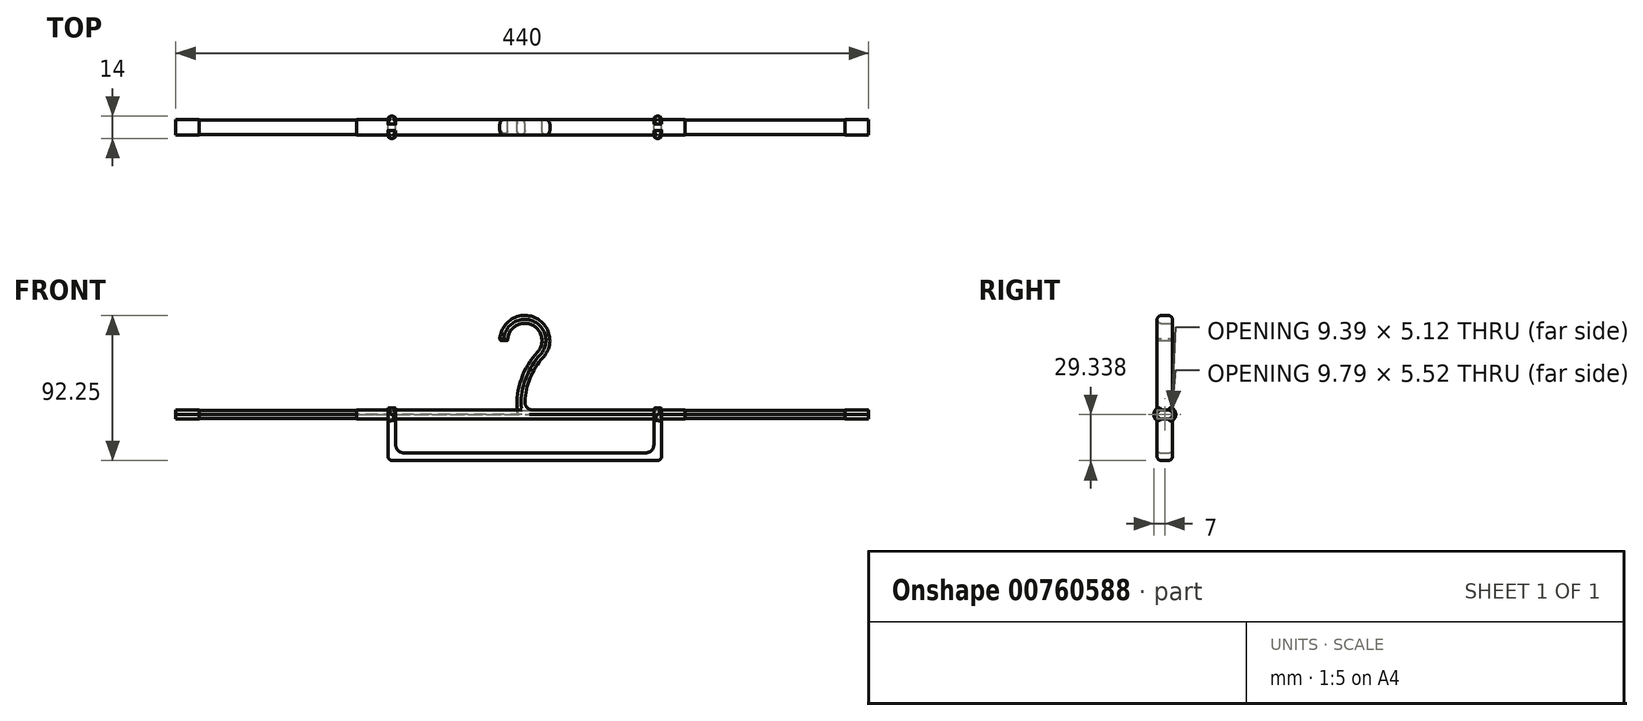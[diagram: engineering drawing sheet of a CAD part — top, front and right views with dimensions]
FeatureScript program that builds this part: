
annotation { "Feature Type Name" : "Feature", "Feature Type Description" : "" }
export const myFeature = defineFeature(function(context is Context, id is Id, definition is map)
    precondition{}
    {
        {
            var Q0;
            Q0=qCreatedBy(makeId("Front.planeOp"),FACE);
            var sketch = newSketch(context, id + "F0", { "sketchPlane" : qUnion([Q0])});
            skCircle(sketch, "E0", {"center": v(0, 49.86) * mm, "radius": 15.9 * mm});
            skCircle(sketch, "E1", {"center": v(0, 49.86) * mm, "radius": 10.9 * mm});
            skLineSegment(sketch, "E2", {"start": v(-15.9, 49.86) * mm, "end": v(-10.9, 49.86) * mm});
            skArc(sketch, "E3", {"start": v(11.73, 39.12) * mm, "mid": v(2.48, 23.62) * mm, "end": v(0.12, 5.72) * mm});
            skArc(sketch, "E4.0", {"start": v(8.04, 42.5) * mm, "mid": v(-2.18, 25.43) * mm, "end": v(-4.9, 5.72) * mm});
            skPoint(sketch, "E5.orphan", {"position": v(0, 9.1) * mm});
            skLineSegment(sketch, "E6", {"start": v(-4.9, 5.72) * mm, "end": v(0.12, 5.72) * mm});
            skLineSegment(sketch, "E7", {"start": v(-4.9, 5.72) * mm, "end": v(-106.71, 5.72) * mm});
            skLineSegment(sketch, "E8", {"start": v(-106.71, 5.72) * mm, "end": v(-106.71, 0) * mm});
            skLineSegment(sketch, "E9", {"start": v(-106.71, 0) * mm, "end": v(-2.39, 0) * mm});
            skPoint(sketch, "E9.endSnap0", {"position": v(-2.39, 5.72) * mm});
            skLineSegment(sketch, "E10", {"start": v(-2.39, 0) * mm, "end": v(-2.39, 5.72) * mm});
            skLineSegment(sketch, "E11.MirrorCS", {"start": v(0.12, 5.72) * mm, "end": v(101.93, 5.72) * mm});
            skLineSegment(sketch, "E12.MirrorCS", {"start": v(101.93, 5.72) * mm, "end": v(101.93, 0) * mm});
            skLineSegment(sketch, "E13.MirrorCS", {"start": v(101.93, 0) * mm, "end": v(-2.39, 0) * mm});
            skLineSegment(sketch, "E14", {"start": v(-86.94, 5.72) * mm, "end": v(-86.94, -26.48) * mm});
            skLineSegment(sketch, "E15", {"start": v(-86.94, -26.48) * mm, "end": v(0, -26.48) * mm});
            skLineSegment(sketch, "E16.0", {"start": v(-81.94, -21.48) * mm, "end": v(0, -21.48) * mm});
            skLineSegment(sketch, "E16.1", {"start": v(-81.94, 5.72) * mm, "end": v(-81.94, -21.48) * mm});
            skLineSegment(sketch, "E17.MirrorCS", {"start": v(81.94, -21.48) * mm, "end": v(0, -21.48) * mm});
            skLineSegment(sketch, "E18.MirrorCS", {"start": v(86.94, -26.48) * mm, "end": v(0, -26.48) * mm});
            skLineSegment(sketch, "E19.MirrorCS", {"start": v(81.94, 5.72) * mm, "end": v(81.94, -21.48) * mm});
            skLineSegment(sketch, "E20.MirrorCS", {"start": v(86.94, 5.72) * mm, "end": v(86.94, -26.48) * mm});
            skSolve(sketch);
        }
        {
            var Q0;
            {var subQ0=sQuery(id+"F0.wireOp",EDGE,"E2");Q0=makeQuery(id+"F0.imprint","IMPRINT",FACE,{"disambiguationData":[TD([[makeQuery(id+"F0.imprint","IMPRINT",EDGE,{"derivedFrom":subQ0}),1.0]])]});}
            var Q1;
            {var subQ6=sQuery(id+"F0.wireOp",EDGE,"E3");Q1=makeQuery(id+"F0.imprint","IMPRINT",FACE,{"disambiguationData":[TD([[makeQuery(id+"F0.imprint","IMPRINT",EDGE,{"derivedFrom":subQ6}),-1.0]])]});}
            extrude(context, id + "F1", {"entities" : qUnion([Q0, Q1]), "endBound" : BoundingType.SYMMETRIC, "depth" : 10 * mm, "offsetDistance" : 25 * mm});
        }
        {
            var Q0;
            {var subQ0=sQuery(id+"F0.wireOp",EDGE,"E10");Q0=makeQuery(id+"F0.imprint","IMPRINT",FACE,{"disambiguationData":[TD([[makeQuery(id+"F0.imprint","IMPRINT",EDGE,{"derivedFrom":subQ0}),1.0]])]});}
            var Q1;
            {var subQ5=sQuery(id+"F0.wireOp",EDGE,"E10");Q1=makeQuery(id+"F0.imprint","IMPRINT",FACE,{"disambiguationData":[TD([[makeQuery(id+"F0.imprint","IMPRINT",EDGE,{"derivedFrom":subQ5}),-1.0]])]});}
            var Q2;
            {var subQ0=sQuery(id+"F0.wireOp",EDGE,"E14");var subQ1=sQuery(id+"F0.wireOp",EDGE,"E7");var subQ2=makeQuery(id+"F0.imprint","INTERSECT",VERTEX,{"derivedFrom":[subQ1,subQ0]});Q2=makeQuery(id+"F0.imprint","IMPRINT",FACE,{"disambiguationData":[TD([[makeQuery(id+"F0.imprint","IMPRINT",EDGE,{"disambiguationData":[TD([[subQ2,1.0]])],"derivedFrom":subQ1}),1.0]])]});}
            var Q3;
            {var subQ0=sQuery(id+"F0.wireOp",EDGE,"E8");Q3=makeQuery(id+"F0.imprint","IMPRINT",FACE,{"disambiguationData":[TD([[makeQuery(id+"F0.imprint","IMPRINT",EDGE,{"derivedFrom":subQ0}),1.0]])]});}
            var Q4;
            {var subQ0=sQuery(id+"F0.wireOp",EDGE,"E19.MirrorCS");var subQ1=sQuery(id+"F0.wireOp",EDGE,"E11.MirrorCS");var subQ2=makeQuery(id+"F0.imprint","INTERSECT",VERTEX,{"derivedFrom":[subQ1,subQ0]});Q4=makeQuery(id+"F0.imprint","IMPRINT",FACE,{"disambiguationData":[TD([[makeQuery(id+"F0.imprint","IMPRINT",EDGE,{"disambiguationData":[TD([[subQ2,-1.0]])],"derivedFrom":subQ1}),-1.0]])]});}
            var Q5;
            {var subQ0=sQuery(id+"F0.wireOp",EDGE,"E12.MirrorCS");Q5=makeQuery(id+"F0.imprint","IMPRINT",FACE,{"disambiguationData":[TD([[makeQuery(id+"F0.imprint","IMPRINT",EDGE,{"derivedFrom":subQ0}),-1.0]])]});}
            extrude(context, id + "F2", {"entities" : qUnion([Q0, Q1, Q2, Q3, Q4, Q5]), "endBound" : BoundingType.SYMMETRIC, "depth" : 10 * mm, "offsetDistance" : 25 * mm});
        }
        {
            var Q0;
            Q0=makeQuery(id+"F1.opExtrude","SWEPT_BODY",BODY,{"disambiguationData":[OSD([sQuery(id+"F0.wireOp",EDGE,"E0"),sQuery(id+"F0.wireOp",EDGE,"E1"),sQuery(id+"F0.wireOp",EDGE,"E2"),sQuery(id+"F0.wireOp",EDGE,"E3"),sQuery(id+"F0.wireOp",EDGE,"E4.0"),sQuery(id+"F0.wireOp",EDGE,"E6")])]});
            var Q1;
            Q1=makeQuery(id+"F2.opExtrude","SWEPT_BODY",BODY,{"disambiguationData":[OSD([sQuery(id+"F0.wireOp",EDGE,"E6"),sQuery(id+"F0.wireOp",EDGE,"E7"),sQuery(id+"F0.wireOp",EDGE,"E8"),sQuery(id+"F0.wireOp",EDGE,"E9"),sQuery(id+"F0.wireOp",EDGE,"E11.MirrorCS"),sQuery(id+"F0.wireOp",EDGE,"E12.MirrorCS"),sQuery(id+"F0.wireOp",EDGE,"E13.MirrorCS")])]});
            booleanBodies(context, id + "F3", {"operationType" : BooleanOperationType.UNION, "tools" : qUnion([Q0, Q1])});
        }
        {
            var Q0;
            {var subQ0=sQuery(id+"F0.wireOp",EDGE,"E15");Q0=makeQuery(id+"F0.imprint","IMPRINT",FACE,{"disambiguationData":[TD([[makeQuery(id+"F0.imprint","IMPRINT",EDGE,{"derivedFrom":subQ0}),1.0]])]});}
            extrude(context, id + "F4", {"entities" : qUnion([Q0]), "endBound" : BoundingType.SYMMETRIC, "depth" : 10 * mm, "offsetDistance" : 25 * mm});
        }
        {
            var Q0;
            Q0=makeQuery(id+"F1.opExtrude","SWEPT_EDGE",EDGE,{"disambiguationData":[OSD([sQuery(id+"F0.wireOp",EDGE,"E4.0"),sQuery(id+"F0.wireOp",EDGE,"E6"),sQuery(id+"F0.wireOp",EDGE,"E7")])]});
            var Q1;
            Q1=makeQuery(id+"F1.opExtrude","SWEPT_EDGE",EDGE,{"disambiguationData":[OSD([sQuery(id+"F0.wireOp",EDGE,"E3"),sQuery(id+"F0.wireOp",EDGE,"E6"),sQuery(id+"F0.wireOp",EDGE,"E11.MirrorCS")])]});
            fillet(context, id + "F5", {"entities" : qUnion([Q0, Q1]), "radius" : 5 * mm, "tangentPropagation" : true, "allowEdgeOverflow" : false});
        }
        {
            var Q0;
            Q0=makeQuery(id+"F1.opExtrude","CAP_EDGE",EDGE,{"disambiguationData":[OSD([sQuery(id+"F0.wireOp",EDGE,"E4.0")])],"isStart":false});
            var Q1;
            Q1=makeQuery(id+"F1.opExtrude","CAP_EDGE",EDGE,{"disambiguationData":[OSD([sQuery(id+"F0.wireOp",EDGE,"E3")])],"isStart":false});
            fillet(context, id + "F6", {"entities" : qUnion([Q0, Q1]), "radius" : 3 * mm, "tangentPropagation" : true, "allowEdgeOverflow" : false});
        }
        {
            var Q0;
            {var subQ0=sQuery(id+"F0.wireOp",EDGE,"E11.MirrorCS");var subQ1=sQuery(id+"F0.wireOp",EDGE,"E7");var subQ2=sQuery(id+"F0.wireOp",EDGE,"E6");var subQ3=sQuery(id+"F0.wireOp",EDGE,"E4.0");Q0=makeQuery(id+"F3.opBoolean","SPLIT",EDGE,{"disambiguationData":[TD([makeQuery(id+"F1.opExtrude","SWEPT_FACE",FACE,{"disambiguationData":[OSD([subQ3])]})])],"derivedFrom":makeQuery(id+"F2.opExtrude","CAP_EDGE",EDGE,{"disambiguationData":[OSD([subQ2,subQ1,subQ0])],"isStart":true})});}
            var Q1;
            Q1=makeQuery(id+"F1.opExtrude","CAP_EDGE",EDGE,{"disambiguationData":[OSD([sQuery(id+"F0.wireOp",EDGE,"E0")])],"isStart":true});
            fillet(context, id + "F7", {"entities" : qUnion([Q0, Q1]), "radius" : 3 * mm, "tangentPropagation" : true, "allowEdgeOverflow" : false});
        }
        {
            var Q0;
            Q0=makeQuery(id+"F2.opExtrude","CAP_EDGE",EDGE,{"disambiguationData":[OSD([sQuery(id+"F0.wireOp",EDGE,"E9"),sQuery(id+"F0.wireOp",EDGE,"E13.MirrorCS")])],"isStart":false});
            var Q1;
            Q1=makeQuery(id+"F2.opExtrude","CAP_EDGE",EDGE,{"disambiguationData":[OSD([sQuery(id+"F0.wireOp",EDGE,"E9"),sQuery(id+"F0.wireOp",EDGE,"E13.MirrorCS")])],"isStart":true});
            fillet(context, id + "F8", {"entities" : qUnion([Q0, Q1]), "radius" : 3 * mm, "tangentPropagation" : true, "allowEdgeOverflow" : false});
        }
        {
            var Q0;
            Q0=makeQuery(id+"F4.opExtrude","CAP_EDGE",EDGE,{"disambiguationData":[OSD([sQuery(id+"F0.wireOp",EDGE,"E14")])],"isStart":false});
            var Q1;
            Q1=makeQuery(id+"F4.opExtrude","CAP_EDGE",EDGE,{"disambiguationData":[OSD([sQuery(id+"F0.wireOp",EDGE,"E14")])],"isStart":true});
            var Q2;
            Q2=makeQuery(id+"F4.opExtrude","CAP_EDGE",EDGE,{"disambiguationData":[OSD([sQuery(id+"F0.wireOp",EDGE,"E15"),sQuery(id+"F0.wireOp",EDGE,"E18.MirrorCS")])],"isStart":false});
            var Q3;
            Q3=makeQuery(id+"F4.opExtrude","CAP_EDGE",EDGE,{"disambiguationData":[OSD([sQuery(id+"F0.wireOp",EDGE,"E15"),sQuery(id+"F0.wireOp",EDGE,"E18.MirrorCS")])],"isStart":true});
            var Q4;
            Q4=makeQuery(id+"F4.opExtrude","CAP_EDGE",EDGE,{"disambiguationData":[OSD([sQuery(id+"F0.wireOp",EDGE,"E20.MirrorCS")])],"isStart":false});
            var Q5;
            Q5=makeQuery(id+"F4.opExtrude","CAP_EDGE",EDGE,{"disambiguationData":[OSD([sQuery(id+"F0.wireOp",EDGE,"E20.MirrorCS")])],"isStart":true});
            var Q6;
            Q6=makeQuery(id+"F4.opExtrude","SWEPT_EDGE",EDGE,{"disambiguationData":[OSD([sQuery(id+"F0.wireOp",EDGE,"E18.MirrorCS"),sQuery(id+"F0.wireOp",EDGE,"E20.MirrorCS")])]});
            var Q7;
            Q7=makeQuery(id+"F4.opExtrude","SWEPT_EDGE",EDGE,{"disambiguationData":[OSD([sQuery(id+"F0.wireOp",EDGE,"E14"),sQuery(id+"F0.wireOp",EDGE,"E15")])]});
            fillet(context, id + "F9", {"entities" : qUnion([Q0, Q1, Q2, Q3, Q4, Q5, Q6, Q7]), "radius" : 3 * mm, "tangentPropagation" : true, "allowEdgeOverflow" : false});
        }
        {
            var Q0;
            Q0=makeQuery(id+"F4.opExtrude","SWEPT_EDGE",EDGE,{"disambiguationData":[OSD([sQuery(id+"F0.wireOp",EDGE,"E16.0"),sQuery(id+"F0.wireOp",EDGE,"E16.1")])]});
            var Q1;
            Q1=makeQuery(id+"F4.opExtrude","SWEPT_EDGE",EDGE,{"disambiguationData":[OSD([sQuery(id+"F0.wireOp",EDGE,"E17.MirrorCS"),sQuery(id+"F0.wireOp",EDGE,"E19.MirrorCS")])]});
            fillet(context, id + "F10", {"entities" : qUnion([Q0, Q1]), "radius" : 5 * mm, "tangentPropagation" : true, "allowEdgeOverflow" : false});
        }
        {
            var Q0;
            Q0=makeQuery(id+"F4.opExtrude","CAP_EDGE",EDGE,{"disambiguationData":[OSD([sQuery(id+"F0.wireOp",EDGE,"E16.1")])],"isStart":false});
            var Q1;
            Q1=makeQuery(id+"F4.opExtrude","CAP_EDGE",EDGE,{"disambiguationData":[OSD([sQuery(id+"F0.wireOp",EDGE,"E19.MirrorCS")])],"isStart":true});
            fillet(context, id + "F11", {"entities" : qUnion([Q0, Q1]), "radius" : 2 * mm, "tangentPropagation" : true, "allowEdgeOverflow" : false});
        }
        {
            var Q0;
            Q0=makeQuery(id+"F2.opExtrude","SWEPT_FACE",FACE,{"disambiguationData":[OSD([sQuery(id+"F0.wireOp",EDGE,"E8")])]});
            var sketch = newSketch(context, id + "F12", { "sketchPlane" : qUnion([Q0])});
            skLineSegment(sketch, "E21.0", {"start": v(2, 5.62) * mm, "end": v(-2, 5.62) * mm});
            skArc(sketch, "E21.1", {"start": v(-4.9, 2.86) * mm, "mid": v(-4, 0.9) * mm, "end": v(-2, 0.1) * mm});
            skLineSegment(sketch, "E21.2", {"start": v(-2, 0.1) * mm, "end": v(2, 0.1) * mm});
            skArc(sketch, "E21.3", {"start": v(-2, 5.62) * mm, "mid": v(-4, 4.82) * mm, "end": v(-4.9, 2.86) * mm});
            skArc(sketch, "E21.4", {"start": v(2, 0.1) * mm, "mid": v(4, 0.9) * mm, "end": v(4.9, 2.86) * mm});
            skArc(sketch, "E21.5", {"start": v(4.9, 2.86) * mm, "mid": v(4, 4.82) * mm, "end": v(2, 5.62) * mm});
            skSolve(sketch);
        }
        {
            var Q0;
            Q0=makeQuery(id+"F12.imprint","IMPRINT",FACE,{"disambiguationData":[TD([[makeQuery(id+"F12.imprint","IMPRINT",EDGE,{"derivedFrom":sQuery(id+"F12.wireOp",EDGE,"E21.0")}),1.0]])]});
            extrude(context, id + "F13", {"entities" : qUnion([Q0]), "operationType" : NewBodyOperationType.REMOVE, "oppositeDirection" : true, "depth" : 250 * mm, "offsetDistance" : 25 * mm});
        }
        {
            var Q0;
            Q0=makeQuery(id+"F12.imprint","IMPRINT",FACE,{"disambiguationData":[TD([[makeQuery(id+"F12.imprint","IMPRINT",EDGE,{"derivedFrom":sQuery(id+"F12.wireOp",EDGE,"E21.0")}),-1.0]])]});
            var sketch = newSketch(context, id + "F14", { "sketchPlane" : qUnion([Q0])});
            skArc(sketch, "E22.0", {"start": v(-4.7, 2.86) * mm, "mid": v(-3.86, 1.04) * mm, "end": v(-2, 0.3) * mm});
            skArc(sketch, "E22.1", {"start": v(2, 0.3) * mm, "mid": v(3.86, 1.04) * mm, "end": v(4.7, 2.86) * mm});
            skArc(sketch, "E22.2", {"start": v(4.7, 2.86) * mm, "mid": v(3.86, 4.68) * mm, "end": v(2, 5.42) * mm});
            skLineSegment(sketch, "E22.3", {"start": v(-2, 0.3) * mm, "end": v(2, 0.3) * mm});
            skLineSegment(sketch, "E22.4", {"start": v(2, 5.42) * mm, "end": v(-2, 5.42) * mm});
            skArc(sketch, "E22.5", {"start": v(-2, 5.42) * mm, "mid": v(-3.86, 4.68) * mm, "end": v(-4.7, 2.86) * mm});
            skSolve(sketch);
        }
        {
            var Q0;
            Q0=makeQuery(id+"F14.imprint","IMPRINT",FACE,{"disambiguationData":[TD([[makeQuery(id+"F14.imprint","IMPRINT",EDGE,{"derivedFrom":sQuery(id+"F14.wireOp",EDGE,"E22.0")}),1.0]])]});
            extrude(context, id + "F15", {"entities" : qUnion([Q0]), "depth" : 100 * mm, "offsetDistance" : 25 * mm});
        }
        {
            var Q0;
            Q0=makeQuery(id+"F14.imprint","IMPRINT",FACE,{"disambiguationData":[TD([[makeQuery(id+"F14.imprint","IMPRINT",EDGE,{"derivedFrom":sQuery(id+"F14.wireOp",EDGE,"E22.0")}),1.0]])]});
            extrude(context, id + "F16", {"entities" : qUnion([Q0]), "operationType" : NewBodyOperationType.ADD, "oppositeDirection" : true, "depth" : 310 * mm, "offsetDistance" : 25 * mm});
        }
        {
            var Q0;
            Q0=makeQuery(id+"F15.opExtrude","CAP_FACE",FACE,{"disambiguationData":[OSD([sQuery(id+"F14.wireOp",EDGE,"E22.0"),sQuery(id+"F14.wireOp",EDGE,"E22.1"),sQuery(id+"F14.wireOp",EDGE,"E22.2"),sQuery(id+"F14.wireOp",EDGE,"E22.3"),sQuery(id+"F14.wireOp",EDGE,"E22.4"),sQuery(id+"F14.wireOp",EDGE,"E22.5")])],"isStart":false});
            var sketch = newSketch(context, id + "F17", { "sketchPlane" : qUnion([Q0])});
            skArc(sketch, "E23.0", {"start": v(-2, 5.62) * mm, "mid": v(-4, 4.82) * mm, "end": v(-4.9, 2.86) * mm});
            skLineSegment(sketch, "E24.0", {"start": v(2, 5.62) * mm, "end": v(-2, 5.62) * mm});
            skArc(sketch, "E25.0", {"start": v(4.9, 2.86) * mm, "mid": v(4, 4.82) * mm, "end": v(2, 5.62) * mm});
            skArc(sketch, "E26.0", {"start": v(2, 0.1) * mm, "mid": v(4, 0.9) * mm, "end": v(4.9, 2.86) * mm});
            skLineSegment(sketch, "E27.0", {"start": v(-2, 0.1) * mm, "end": v(2, 0.1) * mm});
            skArc(sketch, "E28.0", {"start": v(-4.9, 2.86) * mm, "mid": v(-4, 0.9) * mm, "end": v(-2, 0.1) * mm});
            skSolve(sketch);
        }
        {
            var Q0;
            Q0 = qSketchRegion(id + "F17", true);
            extrude(context, id + "F18", {"entities" : qUnion([Q0]), "operationType" : NewBodyOperationType.ADD, "depth" : 5 * mm, "offsetDistance" : 25 * mm});
        }
        {
            var Q0;
            Q0=makeQuery(id+"F16.opExtrude","CAP_FACE",FACE,{"disambiguationData":[OSD([sQuery(id+"F14.wireOp",EDGE,"E22.0"),sQuery(id+"F14.wireOp",EDGE,"E22.1"),sQuery(id+"F14.wireOp",EDGE,"E22.2"),sQuery(id+"F14.wireOp",EDGE,"E22.3"),sQuery(id+"F14.wireOp",EDGE,"E22.4"),sQuery(id+"F14.wireOp",EDGE,"E22.5")])],"isStart":false});
            var sketch = newSketch(context, id + "F19", { "sketchPlane" : qUnion([Q0])});
            skArc(sketch, "E29.0", {"start": v(-2, 5.72) * mm, "mid": v(-4.07, 4.89) * mm, "end": v(-5, 2.86) * mm});
            skLineSegment(sketch, "E30.0", {"start": v(-2, 5.72) * mm, "end": v(2, 5.72) * mm});
            skArc(sketch, "E31.0", {"start": v(5, 2.86) * mm, "mid": v(4.07, 4.89) * mm, "end": v(2, 5.72) * mm});
            skArc(sketch, "E32.0", {"start": v(2, 0) * mm, "mid": v(4.07, 0.83) * mm, "end": v(5, 2.86) * mm});
            skLineSegment(sketch, "E33.0", {"start": v(2, 0.1) * mm, "end": v(-2, 0.1) * mm});
            skArc(sketch, "E34.0", {"start": v(-5, 2.86) * mm, "mid": v(-4.07, 0.83) * mm, "end": v(-2, 0) * mm});
            skLineSegment(sketch, "E35.0", {"start": v(-2, 0) * mm, "end": v(2, 0) * mm});
            skSolve(sketch);
        }
        {
            var Q0;
            Q0 = qSketchRegion(id + "F19", true);
            extrude(context, id + "F20", {"entities" : qUnion([Q0]), "operationType" : NewBodyOperationType.ADD, "depth" : 5 * mm, "offsetDistance" : 25 * mm});
        }
        {
            var Q0;
            Q0=makeQuery(id+"F4.opExtrude","SWEPT_FACE",FACE,{"disambiguationData":[OSD([sQuery(id+"F0.wireOp",EDGE,"E14")])]});
            var sketch = newSketch(context, id + "F21", { "sketchPlane" : qUnion([Q0])});
            skLineSegment(sketch, "E36.0", {"start": v(2, 5.72) * mm, "end": v(-2, 5.72) * mm});
            skArc(sketch, "E37.0", {"start": v(-2, 5.72) * mm, "mid": v(-4.07, 4.89) * mm, "end": v(-5, 2.86) * mm});
            skArc(sketch, "E38.0", {"start": v(-5, 2.86) * mm, "mid": v(-4.07, 0.83) * mm, "end": v(-2, 0) * mm});
            skLineSegment(sketch, "E39.0", {"start": v(2, 0) * mm, "end": v(-2, 0) * mm});
            skArc(sketch, "E40.0", {"start": v(2, 0) * mm, "mid": v(4.07, 0.83) * mm, "end": v(5, 2.86) * mm});
            skArc(sketch, "E41.0", {"start": v(5, 2.86) * mm, "mid": v(4.07, 4.89) * mm, "end": v(2, 5.72) * mm});
            skArc(sketch, "E42.0", {"start": v(7, 2.86) * mm, "mid": v(5.49, 6.3) * mm, "end": v(2, 7.72) * mm});
            skArc(sketch, "E42.1", {"start": v(-2, 7.72) * mm, "mid": v(-5.49, 6.3) * mm, "end": v(-7, 2.86) * mm});
            skArc(sketch, "E42.2", {"start": v(-7, 2.86) * mm, "mid": v(-5.49, -0.59) * mm, "end": v(-2, -2) * mm});
            skLineSegment(sketch, "E42.3", {"start": v(2, -2) * mm, "end": v(-2, -2) * mm});
            skArc(sketch, "E42.4", {"start": v(2, -2) * mm, "mid": v(5.49, -0.59) * mm, "end": v(7, 2.86) * mm});
            skLineSegment(sketch, "E43", {"start": v(-2, 7.72) * mm, "end": v(-2, 5.72) * mm});
            skLineSegment(sketch, "E44", {"start": v(2, 7.72) * mm, "end": v(2, 5.72) * mm});
            skSolve(sketch);
        }
        {
            var Q0;
            {var subQ0=sQuery(id+"F21.wireOp",EDGE,"E40.0");Q0=makeQuery(id+"F21.imprint","IMPRINT",FACE,{"disambiguationData":[TD([[makeQuery(id+"F21.imprint","IMPRINT",EDGE,{"derivedFrom":subQ0}),-1.0]])]});}
            var Q1;
            {var subQ0=sQuery(id+"F21.wireOp",EDGE,"E39.0");Q1=makeQuery(id+"F21.imprint","IMPRINT",FACE,{"disambiguationData":[TD([[makeQuery(id+"F21.imprint","IMPRINT",EDGE,{"derivedFrom":subQ0}),1.0]])]});}
            var Q2;
            Q2=makeQuery(id+"F21.imprint","IMPRINT",FACE,{"disambiguationData":[TD([[makeQuery(id+"F21.imprint","IMPRINT",EDGE,{"derivedFrom":sQuery(id+"F21.wireOp",EDGE,"E37.0")}),-1.0]])]});
            extrude(context, id + "F22", {"entities" : qUnion([Q0, Q1, Q2]), "operationType" : NewBodyOperationType.ADD, "oppositeDirection" : true, "depth" : 5 * mm, "offsetDistance" : 25 * mm});
        }
        {
            var Q0;
            Q0=makeQuery(id+"F4.opExtrude","SWEPT_FACE",FACE,{"disambiguationData":[OSD([sQuery(id+"F0.wireOp",EDGE,"E20.MirrorCS")])]});
            var sketch = newSketch(context, id + "F23", { "sketchPlane" : qUnion([Q0])});
            skArc(sketch, "E45.0.0", {"start": v(-7, 2.86) * mm, "mid": v(-5.83, -0.22) * mm, "end": v(-3, -1.9) * mm});
            skArc(sketch, "E45.0.4", {"start": v(3, -1.9) * mm, "mid": v(5.83, -0.22) * mm, "end": v(7, 2.86) * mm});
            skArc(sketch, "E45.0.5", {"start": v(7, 2.86) * mm, "mid": v(5.49, 6.3) * mm, "end": v(2, 7.72) * mm});
            skLineSegment(sketch, "E45.0.6", {"start": v(2, 7.72) * mm, "end": v(2, 5.72) * mm});
            skArc(sketch, "E45.0.7", {"start": v(2, 5.72) * mm, "mid": v(4.07, 4.89) * mm, "end": v(5, 2.86) * mm});
            skArc(sketch, "E45.0.8", {"start": v(5, 2.86) * mm, "mid": v(4.07, 0.83) * mm, "end": v(2, 0) * mm});
            skLineSegment(sketch, "E45.0.9", {"start": v(2, 0) * mm, "end": v(-2, 0) * mm});
            skArc(sketch, "E45.0.10", {"start": v(-2, 0) * mm, "mid": v(-4.07, 0.83) * mm, "end": v(-5, 2.86) * mm});
            skArc(sketch, "E45.0.11", {"start": v(-5, 2.86) * mm, "mid": v(-4.07, 4.89) * mm, "end": v(-2, 5.72) * mm});
            skLineSegment(sketch, "E45.0.12", {"start": v(-2, 5.72) * mm, "end": v(-2, 7.72) * mm});
            skArc(sketch, "E45.0.13", {"start": v(-2, 7.72) * mm, "mid": v(-5.49, 6.3) * mm, "end": v(-7, 2.86) * mm});
            skArc(sketch, "E46.0", {"start": v(-2, -2) * mm, "mid": v(-5.45, -0.62) * mm, "end": v(-7, 2.76) * mm});
            skLineSegment(sketch, "E46.1", {"start": v(2, -2) * mm, "end": v(-2, -2) * mm});
            skArc(sketch, "E46.2", {"start": v(7, 2.76) * mm, "mid": v(5.45, -0.62) * mm, "end": v(2, -2) * mm});
            skSolve(sketch);
        }
        {
            var Q0;
            {var subQ5=sQuery(id+"F23.wireOp",EDGE,"E45.0.0");Q0=makeQuery(id+"F23.imprint","IMPRINT",FACE,{"disambiguationData":[TD([[makeQuery(id+"F23.imprint","IMPRINT",EDGE,{"derivedFrom":subQ5}),1.0]])]});}
            var Q1;
            {var subQ0=sQuery(id+"F23.wireOp",EDGE,"E45.0.9");Q1=makeQuery(id+"F23.imprint","IMPRINT",FACE,{"disambiguationData":[TD([[makeQuery(id+"F23.imprint","IMPRINT",EDGE,{"derivedFrom":subQ0}),-1.0]])]});}
            var Q2;
            {var subQ1=sQuery(id+"F23.wireOp",EDGE,"E45.0.4");Q2=makeQuery(id+"F23.imprint","IMPRINT",FACE,{"disambiguationData":[TD([[makeQuery(id+"F23.imprint","IMPRINT",EDGE,{"derivedFrom":subQ1}),1.0]])]});}
            extrude(context, id + "F24", {"entities" : qUnion([Q0, Q1, Q2]), "operationType" : NewBodyOperationType.ADD, "oppositeDirection" : true, "depth" : 5 * mm, "offsetDistance" : 25 * mm});
        }
        {
            var Q0;
            Q0=makeQuery(id+"F22.opExtrude","CAP_EDGE",EDGE,{"disambiguationData":[OSD([sQuery(id+"F21.wireOp",EDGE,"E42.4")])],"isStart":true});
            var Q1;
            Q1=makeQuery(id+"F22.opExtrude","CAP_EDGE",EDGE,{"disambiguationData":[OSD([sQuery(id+"F21.wireOp",EDGE,"E42.0")])],"isStart":false});
            var Q2;
            Q2=makeQuery(id+"F22.opExtrude","CAP_EDGE",EDGE,{"disambiguationData":[OSD([sQuery(id+"F21.wireOp",EDGE,"E42.2")])],"isStart":true});
            var Q3;
            Q3=makeQuery(id+"F22.opExtrude","CAP_EDGE",EDGE,{"disambiguationData":[OSD([sQuery(id+"F21.wireOp",EDGE,"E42.2")])],"isStart":false});
            var Q4;
            Q4=makeQuery(id+"F24.opExtrude","CAP_EDGE",EDGE,{"disambiguationData":[OSD([sQuery(id+"F23.wireOp",EDGE,"E45.0.13")])],"isStart":false});
            var Q5;
            Q5=makeQuery(id+"F24.opExtrude","CAP_EDGE",EDGE,{"disambiguationData":[OSD([sQuery(id+"F23.wireOp",EDGE,"E45.0.0"),sQuery(id+"F23.wireOp",EDGE,"E46.0")])],"isStart":true});
            var Q6;
            Q6=makeQuery(id+"F24.opExtrude","CAP_EDGE",EDGE,{"disambiguationData":[OSD([sQuery(id+"F23.wireOp",EDGE,"E45.0.5")])],"isStart":false});
            var Q7;
            Q7=makeQuery(id+"F24.opExtrude","CAP_EDGE",EDGE,{"disambiguationData":[OSD([sQuery(id+"F23.wireOp",EDGE,"E45.0.5")])],"isStart":true});
            var Q8;
            Q8=makeQuery(id+"F24.opExtrude","SWEPT_EDGE",EDGE,{"disambiguationData":[OSD([sQuery(id+"F23.wireOp",EDGE,"E45.0.5"),sQuery(id+"F23.wireOp",EDGE,"E45.0.6")])]});
            var Q9;
            Q9=makeQuery(id+"F24.opExtrude","SWEPT_EDGE",EDGE,{"disambiguationData":[OSD([sQuery(id+"F23.wireOp",EDGE,"E45.0.12"),sQuery(id+"F23.wireOp",EDGE,"E45.0.13")])]});
            var Q10;
            Q10=makeQuery(id+"F22.opExtrude","SWEPT_EDGE",EDGE,{"disambiguationData":[OSD([sQuery(id+"F21.wireOp",EDGE,"E42.1"),sQuery(id+"F21.wireOp",EDGE,"E43")])]});
            var Q11;
            Q11=makeQuery(id+"F22.opExtrude","SWEPT_EDGE",EDGE,{"disambiguationData":[OSD([sQuery(id+"F21.wireOp",EDGE,"E42.0"),sQuery(id+"F21.wireOp",EDGE,"E44")])]});
            fillet(context, id + "F25", {"entities" : qUnion([Q0, Q1, Q2, Q3, Q4, Q5, Q6, Q7, Q8, Q9, Q10, Q11]), "radius" : 2 * mm, "tangentPropagation" : true, "allowEdgeOverflow" : false});
        }
        {
            var Q0;
            Q0=makeQuery(id+"F1.opExtrude","SWEPT_EDGE",EDGE,{"disambiguationData":[OSD([sQuery(id+"F0.wireOp",EDGE,"E0"),sQuery(id+"F0.wireOp",EDGE,"E2")])]});
            fillet(context, id + "F26", {"entities" : qUnion([Q0]), "radius" : 1 * mm, "tangentPropagation" : true, "allowEdgeOverflow" : false});
        }
        {
            var Q0;
            Q0=makeQuery(id+"F18.opExtrude","CAP_FACE",FACE,{"disambiguationData":[OSD([sQuery(id+"F17.wireOp",EDGE,"E23.0"),sQuery(id+"F17.wireOp",EDGE,"E24.0"),sQuery(id+"F17.wireOp",EDGE,"E25.0"),sQuery(id+"F17.wireOp",EDGE,"E26.0"),sQuery(id+"F17.wireOp",EDGE,"E27.0"),sQuery(id+"F17.wireOp",EDGE,"E28.0")])],"isStart":false});
            extrude(context, id + "F27", {"entities" : qUnion([Q0]), "operationType" : NewBodyOperationType.ADD, "depth" : 10 * mm, "offsetDistance" : 25 * mm});
        }
        {
            var Q0;
            Q0=makeQuery(id+"F20.opExtrude","CAP_FACE",FACE,{"disambiguationData":[OSD([sQuery(id+"F19.wireOp",EDGE,"E29.0"),sQuery(id+"F19.wireOp",EDGE,"E30.0"),sQuery(id+"F19.wireOp",EDGE,"E31.0"),sQuery(id+"F19.wireOp",EDGE,"E32.0"),sQuery(id+"F19.wireOp",EDGE,"E34.0"),sQuery(id+"F19.wireOp",EDGE,"E35.0")])],"isStart":false});
            extrude(context, id + "F28", {"entities" : qUnion([Q0]), "operationType" : NewBodyOperationType.ADD, "depth" : 10 * mm, "offsetDistance" : 25 * mm});
        }
    });
